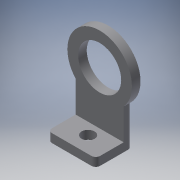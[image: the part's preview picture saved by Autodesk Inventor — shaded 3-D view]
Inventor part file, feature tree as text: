
AUTODESK INVENTOR PART (.ipt)
format: ipt  version: 2016 (Build 200138000, 138)  size: 145,408 bytes
history: native  units: in
note: dims shown in document units (in); Inventor stores cm internally (conversion verified against a paired STEP export)
features: extrude x4, sketch x4, reference x2, fillet x1
ambient origin geometry x8: Origin, YZ Plane, XZ Plane, XY Plane, X Axis, Y Axis, Z Axis, Center Point
bodies: Solid1 (feature_tree)
feature tree (11):
  extrude  "Extrusion1"  Depth=0.3937in
  extrude  "Extrusion2"  Depth=0.0787in TaperAngle=0.0deg
  extrude  "Extrusion5"  Depth=0.3346in
  extrude  "Extrusion6"  Depth=0.0394in
  fillet  "Fillet1"  Radius=0.1181in
  sketch  "Sketch1"  dims[d0=0.3937in d1=0.5906in]
  reference  "Reference1"
  sketch  "Sketch2"  dims[d2=0.0787in d3=0.0in d4=0.0787in d5=0.0in]
  reference  "Reference2"
  sketch  "Sketch5"  dims[d13=0.0984in d14=0.3346in]
  sketch  "Sketch6"  dims[d15=0.0787in d16=0.0in d17=0.15in d18=0.1181in d19=0.0787in d20=0.0in d21=0.0394in]
